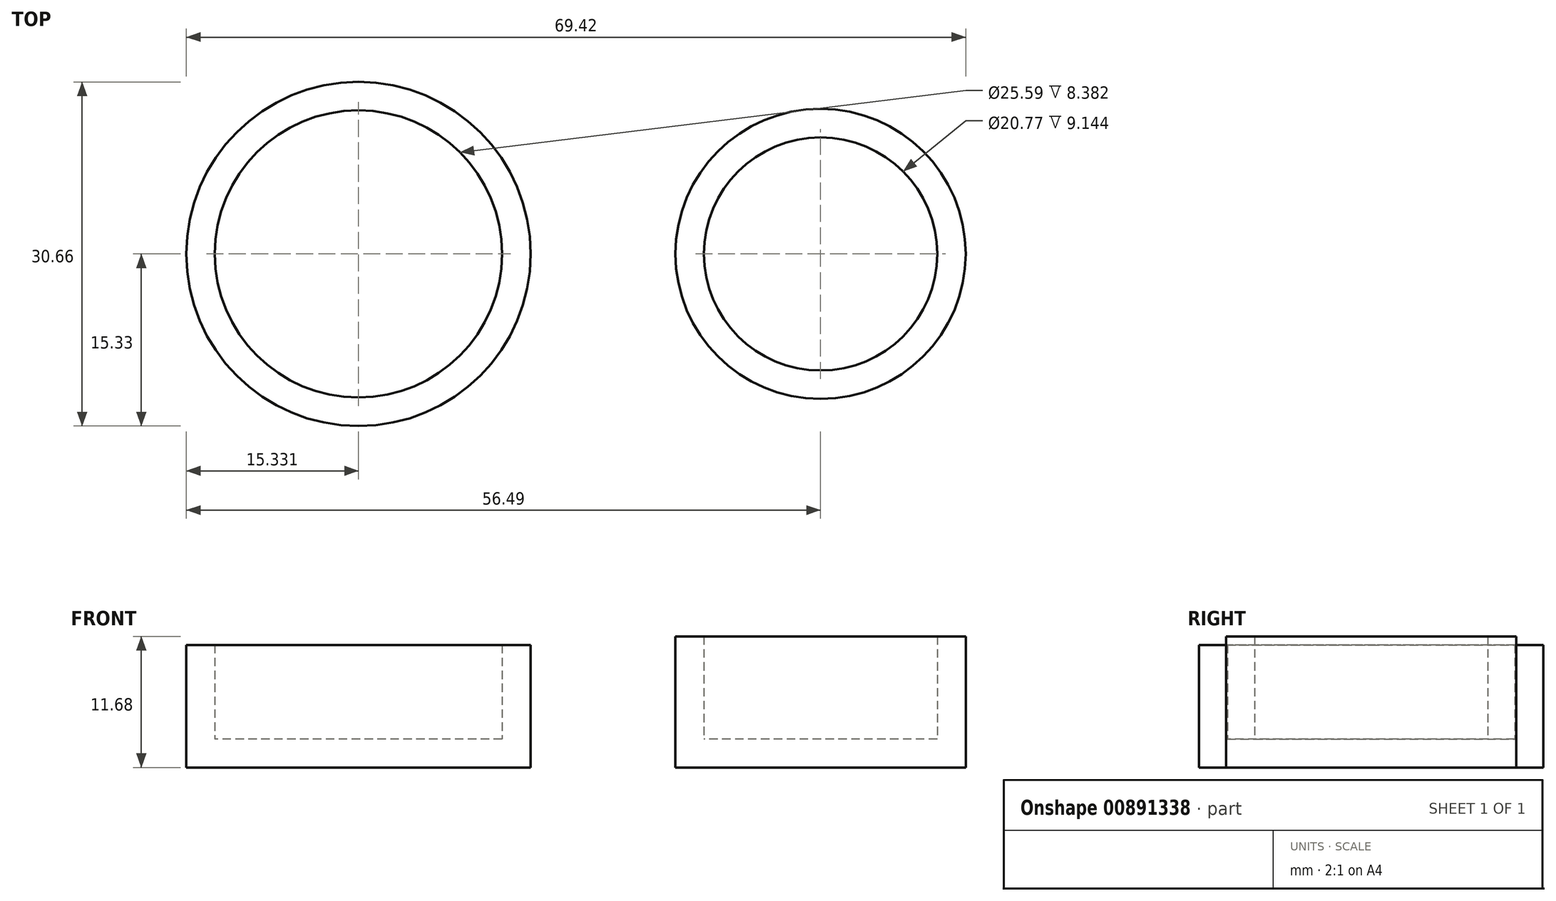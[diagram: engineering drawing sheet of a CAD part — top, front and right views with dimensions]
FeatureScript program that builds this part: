
annotation { "Feature Type Name" : "Feature", "Feature Type Description" : "" }
export const myFeature = defineFeature(function(context is Context, id is Id, definition is map)
    precondition{}
    {
        {
            var Q0;
            Q0=qCreatedBy(makeId("Top.planeOp"),FACE);
            var sketch = newSketch(context, id + "F0", { "sketchPlane" : qUnion([Q0])});
            skCircle(sketch, "E0", {"center": v(0, 0) * mm, "radius": 12.93 * mm});
            skSolve(sketch);
        }
        {
            var Q0;
            Q0 = qSketchRegion(id + "F0", true);
            extrude(context, id + "F1", {"entities" : qUnion([Q0]), "depth" : 7.11 * mm, "offsetDistance" : 25.4 * mm});
        }
        {
            var Q0;
            Q0=makeQuery(id+"F1.opExtrude","CAP_FACE",FACE,{"disambiguationData":[OSD([sQuery(id+"F0.wireOp",EDGE,"E0")])],"isStart":false});
            shell(context, id + "F2", {"entities" : qUnion([Q0]), "thickness" : 2.54 * mm});
        }
        {
            var Q0;
            Q0=makeQuery(id+"F1.opExtrude","CAP_FACE",FACE,{"disambiguationData":[OSD([sQuery(id+"F0.wireOp",EDGE,"E0")])],"isStart":false});
            extrude(context, id + "F3", {"entities" : qUnion([Q0]), "operationType" : NewBodyOperationType.ADD, "depth" : 4.57 * mm, "offsetDistance" : 25.4 * mm});
        }
        {
            var Q0;
            Q0=qCreatedBy(makeId("Top.planeOp"),FACE);
            var sketch = newSketch(context, id + "F4", { "sketchPlane" : qUnion([Q0])});
            skCircle(sketch, "E1", {"center": v(-41.16, 0) * mm, "radius": 15.33 * mm});
            skSolve(sketch);
        }
        {
            var Q0;
            Q0=makeQuery(id+"F4.imprint","IMPRINT",FACE,{"disambiguationData":[TD([[makeQuery(id+"F4.imprint","IMPRINT",EDGE,{"derivedFrom":sQuery(id+"F4.wireOp",EDGE,"E1")}),1.0]])]});
            extrude(context, id + "F5", {"entities" : qUnion([Q0]), "depth" : 10.92 * mm, "offsetDistance" : 25.4 * mm});
        }
        {
            var Q0;
            Q0=makeQuery(id+"F5.opExtrude","CAP_FACE",FACE,{"disambiguationData":[OSD([sQuery(id+"F4.wireOp",EDGE,"E1")])],"isStart":false});
            shell(context, id + "F6", {"entities" : qUnion([Q0]), "thickness" : 2.54 * mm});
        }
    });
